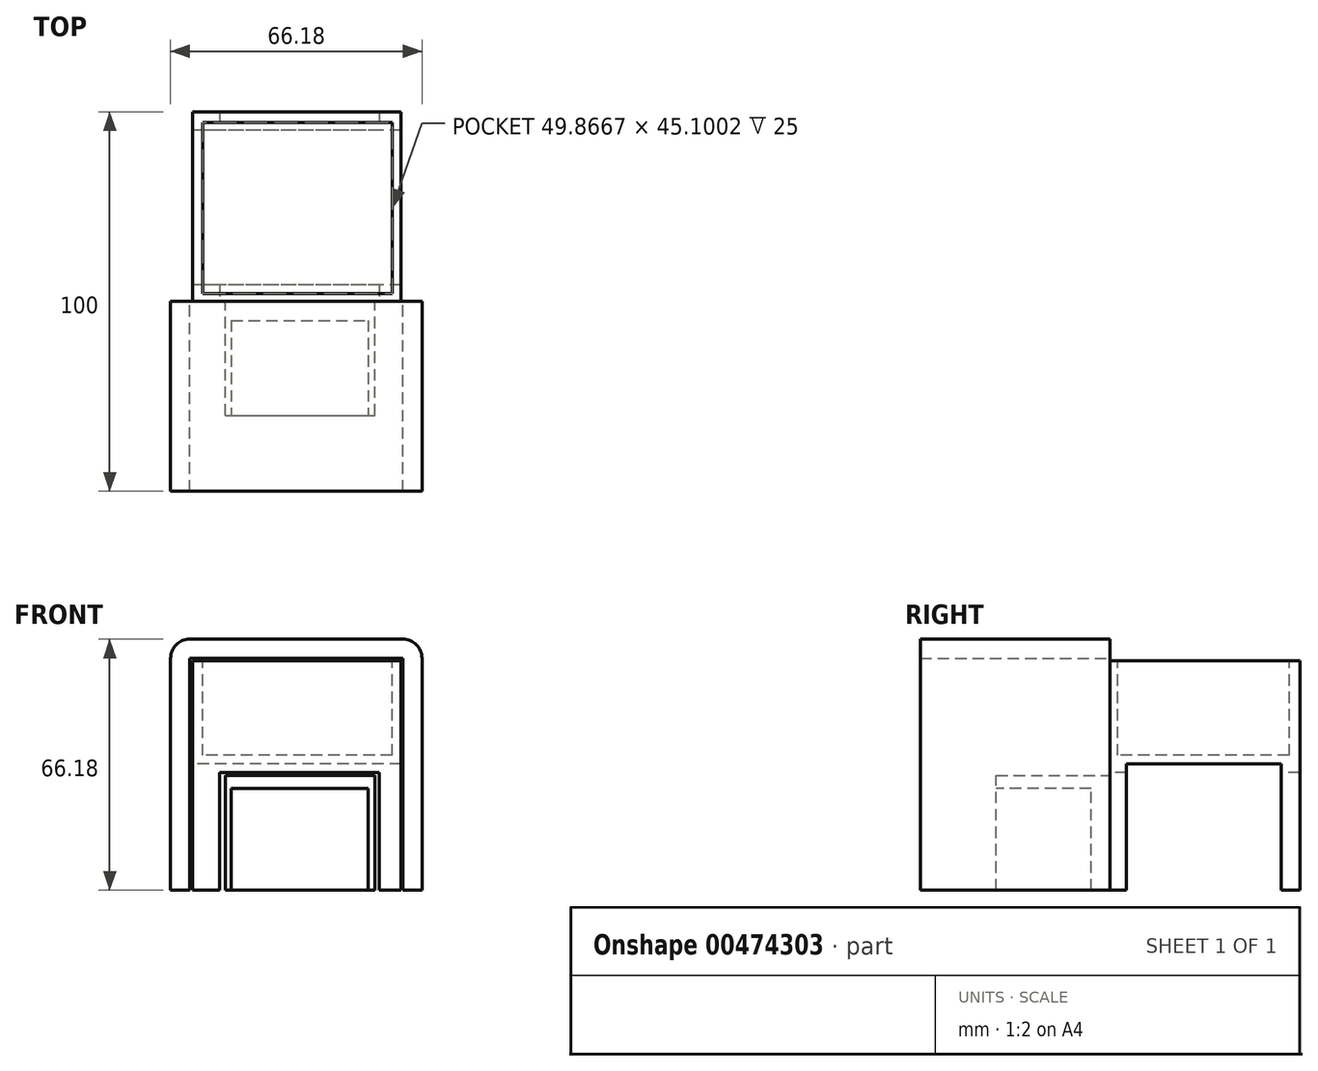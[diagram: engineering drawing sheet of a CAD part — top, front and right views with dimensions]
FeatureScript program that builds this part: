
annotation { "Feature Type Name" : "Feature", "Feature Type Description" : "" }
export const myFeature = defineFeature(function(context is Context, id is Id, definition is map)
    precondition{}
    {
        {
            var Q0;
            Q0=qCreatedBy(makeId("Front.planeOp"),FACE);
            var sketch = newSketch(context, id + "F0", { "sketchPlane" : qUnion([Q0])});
            skLineSegment(sketch, "E0.bottom", {"start": v(0, 0) * mm, "end": v(5, 0) * mm});
            skLineSegment(sketch, "E0.top", {"start": v(5, 66.18) * mm, "end": v(61.18, 66.18) * mm});
            skLineSegment(sketch, "E0.left", {"start": v(0, 0) * mm, "end": v(0, 61.18) * mm});
            skLineSegment(sketch, "E0.right", {"start": v(66.18, 0) * mm, "end": v(66.18, 61.18) * mm});
            skLineSegment(sketch, "E1.0", {"start": v(61.18, 0) * mm, "end": v(61.18, 61.18) * mm});
            skLineSegment(sketch, "E1.1", {"start": v(5, 61.18) * mm, "end": v(61.18, 61.18) * mm});
            skLineSegment(sketch, "E1.2", {"start": v(5, 0) * mm, "end": v(5, 61.18) * mm});
            skLineSegment(sketch, "E2.trimOffspring", {"start": v(61.18, 0) * mm, "end": v(66.18, 0) * mm});
            skPoint(sketch, "E3.visualSharp", {"position": v(66.18, 66.18) * mm});
            skArc(sketch, "E3.filletArc", {"start": v(66.18, 61.18) * mm, "mid": v(64.71, 64.71) * mm, "end": v(61.18, 66.18) * mm});
            skPoint(sketch, "E4.visualSharp", {"position": v(0, 66.18) * mm});
            skArc(sketch, "E4.filletArc", {"start": v(5, 66.18) * mm, "mid": v(1.46, 64.71) * mm, "end": v(0, 61.18) * mm});
            skSolve(sketch);
        }
        {
            var Q0;
            Q0=qCreatedBy(makeId("Front.planeOp"),FACE);
            var sketch = newSketch(context, id + "F1", { "sketchPlane" : qUnion([Q0])});
            skLineSegment(sketch, "E5.bottom", {"start": v(14.45, 0) * mm, "end": v(53.75, 0) * mm});
            skLineSegment(sketch, "E5.top", {"start": v(14.45, 30.21) * mm, "end": v(53.75, 30.21) * mm});
            skLineSegment(sketch, "E5.right", {"start": v(53.75, 0) * mm, "end": v(53.75, 30.21) * mm});
            skLineSegment(sketch, "E6", {"start": v(14.45, 30.21) * mm, "end": v(14.45, 0) * mm});
            skLineSegment(sketch, "E7.bottom", {"start": v(5.78, 60.54) * mm, "end": v(60.69, 60.54) * mm});
            skLineSegment(sketch, "E7.top", {"start": v(12.94, 31.07) * mm, "end": v(54.98, 31.07) * mm});
            skLineSegment(sketch, "E7.left", {"start": v(5.78, 60.54) * mm, "end": v(5.78, 31.07) * mm});
            skLineSegment(sketch, "E7.right", {"start": v(60.69, 60.54) * mm, "end": v(60.69, 31.07) * mm});
            skLineSegment(sketch, "E8.top", {"start": v(5.78, 0) * mm, "end": v(12.94, 0) * mm});
            skLineSegment(sketch, "E8.left", {"start": v(5.78, 31.07) * mm, "end": v(5.78, 0) * mm});
            skLineSegment(sketch, "E8.right", {"start": v(12.94, 31.07) * mm, "end": v(12.94, 0) * mm});
            skLineSegment(sketch, "E9.top", {"start": v(60.69, 0) * mm, "end": v(54.98, 0) * mm});
            skLineSegment(sketch, "E9.left", {"start": v(60.69, 31.07) * mm, "end": v(60.69, 0) * mm});
            skLineSegment(sketch, "E9.right", {"start": v(54.98, 31.07) * mm, "end": v(54.98, 0) * mm});
            skSolve(sketch);
        }
        {
            var Q0;
            Q0=makeQuery(id+"F0.imprint","IMPRINT",FACE,{"disambiguationData":[TD([[makeQuery(id+"F0.imprint","IMPRINT",EDGE,{"derivedFrom":sQuery(id+"F0.wireOp",EDGE,"E0.bottom")}),1.0]])]});
            extrude(context, id + "F2", {"entities" : qUnion([Q0]), "depth" : 50 * mm});
        }
        {
            var Q0;
            Q0=makeQuery(id+"F1.imprint","IMPRINT",FACE,{"disambiguationData":[TD([[makeQuery(id+"F1.imprint","IMPRINT",EDGE,{"derivedFrom":sQuery(id+"F1.wireOp",EDGE,"E7.bottom")}),-1.0]])]});
            extrude(context, id + "F3", {"entities" : qUnion([Q0]), "oppositeDirection" : true, "depth" : 50 * mm});
        }
        {
            var Q0;
            Q0=qCreatedBy(makeId("Right.planeOp"),FACE);
            var sketch = newSketch(context, id + "F4", { "sketchPlane" : qUnion([Q0])});
            skLineSegment(sketch, "E10.bottom", {"start": v(45.08, 0) * mm, "end": v(4.33, 0) * mm});
            skLineSegment(sketch, "E10.top", {"start": v(45.08, 33.38) * mm, "end": v(4.33, 33.38) * mm});
            skLineSegment(sketch, "E10.left", {"start": v(45.08, 0) * mm, "end": v(45.08, 33.38) * mm});
            skLineSegment(sketch, "E10.right", {"start": v(4.33, 0) * mm, "end": v(4.33, 33.38) * mm});
            skSolve(sketch);
        }
        {
            var Q0;
            Q0=makeQuery(id+"F4.imprint","IMPRINT",FACE,{"disambiguationData":[TD([[makeQuery(id+"F4.imprint","IMPRINT",EDGE,{"derivedFrom":sQuery(id+"F4.wireOp",EDGE,"E10.bottom")}),-1.0]])]});
            extrude(context, id + "F5", {"entities" : qUnion([Q0]), "operationType" : NewBodyOperationType.REMOVE, "depth" : 90 * mm});
        }
        {
            var Q0;
            Q0=makeQuery(id+"F1.imprint","IMPRINT",FACE,{"disambiguationData":[TD([[makeQuery(id+"F1.imprint","IMPRINT",EDGE,{"derivedFrom":sQuery(id+"F1.wireOp",EDGE,"E5.bottom")}),1.0]])]});
            extrude(context, id + "F6", {"entities" : qUnion([Q0]), "depth" : 30 * mm});
        }
        {
            var Q0;
            Q0=makeQuery(id+"F3.opExtrude","SWEPT_FACE",FACE,{"disambiguationData":[OSD([sQuery(id+"F1.wireOp",EDGE,"E7.bottom")])]});
            var sketch = newSketch(context, id + "F7", { "sketchPlane" : qUnion([Q0])});
            skLineSegment(sketch, "E11.bottom", {"start": v(58.34, 47.15) * mm, "end": v(8.47, 47.15) * mm});
            skLineSegment(sketch, "E11.top", {"start": v(58.34, 2.05) * mm, "end": v(8.47, 2.05) * mm});
            skLineSegment(sketch, "E11.left", {"start": v(58.34, 47.15) * mm, "end": v(58.34, 2.05) * mm});
            skLineSegment(sketch, "E11.right", {"start": v(8.47, 47.15) * mm, "end": v(8.47, 2.05) * mm});
            skSolve(sketch);
        }
        {
            var Q0;
            Q0=makeQuery(id+"F7.imprint","IMPRINT",FACE,{"disambiguationData":[TD([[makeQuery(id+"F7.imprint","IMPRINT",EDGE,{"derivedFrom":sQuery(id+"F7.wireOp",EDGE,"E11.bottom")}),1.0]])]});
            extrude(context, id + "F8", {"entities" : qUnion([Q0]), "operationType" : NewBodyOperationType.REMOVE, "oppositeDirection" : true, "depth" : 25 * mm});
        }
        {
            var Q0;
            Q0=makeQuery(id+"F6.opExtrude","CAP_FACE",FACE,{"disambiguationData":[OSD([sQuery(id+"F1.wireOp",EDGE,"E5.bottom"),sQuery(id+"F1.wireOp",EDGE,"E5.top"),sQuery(id+"F1.wireOp",EDGE,"E5.right"),sQuery(id+"F1.wireOp",EDGE,"E6")])],"isStart":false});
            var sketch = newSketch(context, id + "F9", { "sketchPlane" : qUnion([Q0])});
            skLineSegment(sketch, "E12.bottom", {"start": v(15.97, 0) * mm, "end": v(52.06, 0) * mm});
            skLineSegment(sketch, "E12.top", {"start": v(15.97, 26.89) * mm, "end": v(52.06, 26.89) * mm});
            skLineSegment(sketch, "E12.left", {"start": v(15.97, 0) * mm, "end": v(15.97, 26.89) * mm});
            skLineSegment(sketch, "E12.right", {"start": v(52.06, 0) * mm, "end": v(52.06, 26.89) * mm});
            skSolve(sketch);
        }
        {
            var Q0;
            Q0=makeQuery(id+"F9.imprint","IMPRINT",FACE,{"disambiguationData":[TD([[makeQuery(id+"F9.imprint","IMPRINT",EDGE,{"derivedFrom":sQuery(id+"F9.wireOp",EDGE,"E12.bottom")}),1.0]])]});
            extrude(context, id + "F10", {"entities" : qUnion([Q0]), "operationType" : NewBodyOperationType.REMOVE, "oppositeDirection" : true, "depth" : 25 * mm});
        }
    });
